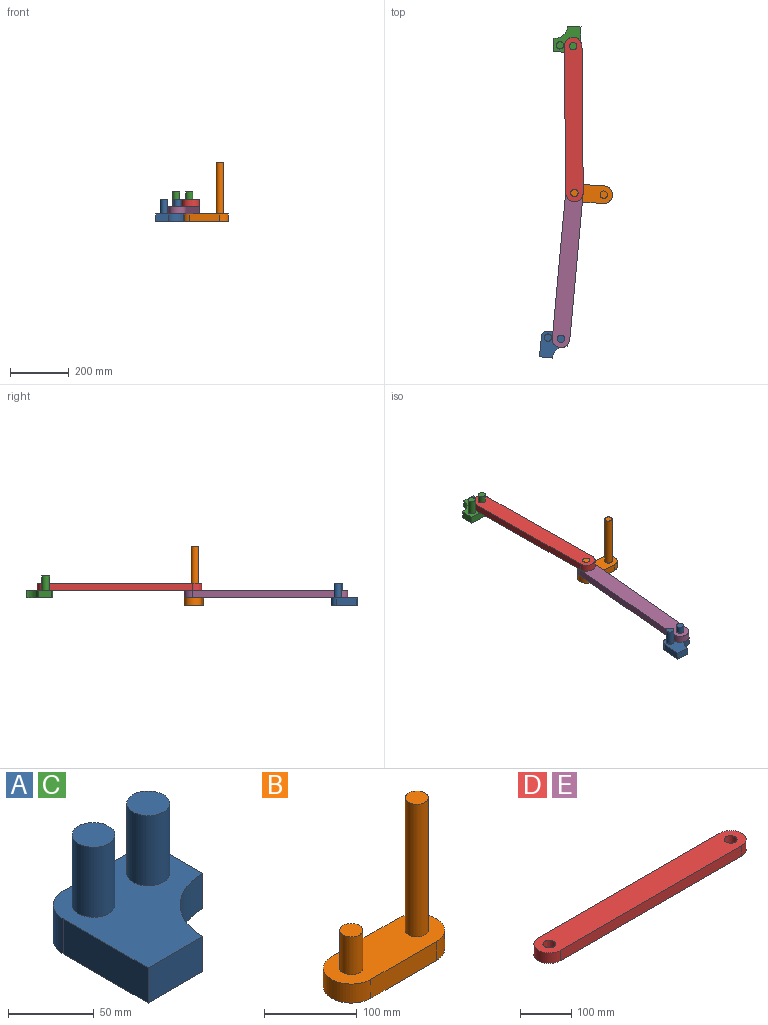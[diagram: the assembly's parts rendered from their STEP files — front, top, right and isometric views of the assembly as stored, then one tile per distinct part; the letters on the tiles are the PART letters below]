
ASSEMBLY  parts=5 mates=5
PART A: 12 faces, bbox 90x90x75 mm
  f0: plane 45x25mm, normal (1,0,0), area 1125mm2, adj f1,f4,f5,f6
  f1: plane 70x25mm, normal (0,1,0), area 1750mm2, adj f0,f4,f5,f7
  f2: plane 70x25mm, normal (-1,0,0), area 1750mm2, adj f3,f4,f5,f7
  f3: plane 45x25mm, normal (0,-1,0), area 1125mm2, adj f2,f4,f5,f6
  f4: plane 90x90mm, normal (0,0,1), area 5442mm2, adj f0,f1,f2,f3,f6,f7,f8,f10
  f5: plane 90x90mm, normal (0,0,-1), area 6423.7mm2, adj f0,f1,f2,f3,f6,f7
  f6: cylinder r=45mm len=45mm, axis (0,0,1), area 1767.1mm2, adj f0,f3,f4,f5
  f7: cylinder r=20mm len=25mm, axis (0,0,-1), area 785.4mm2, adj f1,f2,f4,f5
  f8: cylinder r=12.5mm len=50mm, axis (0,0,-1), area 3927mm2, adj f4,f9
  f9: plane 25x25mm, normal (0,0,1), area 490.9mm2, adj f8
  f10: cylinder r=12.5mm len=50mm, axis (0,0,-1), area 3927mm2, adj f4,f11
  f11: plane 25x25mm, normal (0,0,1), area 490.9mm2, adj f10
PART B: 10 faces, bbox 160x60x200 mm
  f0: plane 100x25mm, normal (0,1,0), area 2500mm2, adj f1,f3,f4,f5
  f1: cylinder r=30mm len=60mm, axis (0,0,-1), area 2356.2mm2, adj f0,f2,f4,f5
  f2: plane 100x25mm, normal (0,-1,0), area 2500mm2, adj f1,f3,f4,f5
  f3: cylinder r=30mm len=60mm, axis (0,0,-1), area 2356.2mm2, adj f0,f2,f4,f5
  f4: plane 160x60mm, normal (0,0,1), area 7845.7mm2, adj f0,f1,f2,f3,f6,f8
  f5: plane 160x60mm, normal (0,0,-1), area 8827.4mm2, adj f0,f1,f2,f3
  f6: cylinder r=12.5mm len=175mm, axis (0,0,-1), area 13744.5mm2, adj f4,f7
  f7: plane 25x25mm, normal (0,0,1), area 490.9mm2, adj f6
  f8: cylinder r=12.5mm len=50mm, axis (0,0,-1), area 3927mm2, adj f4,f9
  f9: plane 25x25mm, normal (0,0,1), area 490.9mm2, adj f8
PART C: same geometry as A
PART D: 8 faces, bbox 560x60x25 mm
  f0: plane 500x25mm, normal (0,1,0), area 12500mm2, adj f1,f5,f6,f7
  f1: cylinder r=30mm len=60mm, axis (0,0,-1), area 2356.2mm2, adj f0,f2,f6,f7
  f2: plane 500x25mm, normal (0,-1,0), area 12500mm2, adj f1,f5,f6,f7
  f3: cylinder r=12.5mm len=25mm, axis (0,0,-1), area 1963.5mm2, adj f6,f7
  f4: cylinder r=12.5mm len=25mm, axis (0,0,-1), area 1963.5mm2, adj f6,f7
  f5: cylinder r=30mm len=60mm, axis (0,0,-1), area 2356.2mm2, adj f0,f2,f6,f7
  f6: plane 560x60mm, normal (0,0,1), area 31845.7mm2, adj f0,f1,f2,f3,f4,f5
  f7: plane 560x60mm, normal (0,0,-1), area 31845.7mm2, adj f0,f1,f2,f3,f4,f5
PART E: same geometry as D
PLACE A rot(axis=(0,0,-1),5.2deg) t=(-148.94,-319.14,45.08)mm
PLACE B rot(axis=(0,0,-1),3.7deg) t=(-27.62,87.4,45.08)mm fixed
PLACE C rot(axis=(0,0,1),176.4deg) t=(-98.25,506.04,70.08)mm
PLACE D rot(axis=(0,0,-1),89.5deg) t=(-165.76,539.5,95.08)mm
PLACE E rot(axis=(0,0,1),84.8deg) t=(-34.36,-364.8,70.08)mm
MATE revolute D.f4 <-> B.f8  axis (0,0,-1) through (-77.52,90.63,120.08)mm
MATE parallel E.f6 <-> D.f6  axis (0,0,1) through (-100.3,-158.33,95.08)mm
MATE revolute A.f8 <-> E.f1  axis (0,0,-1) through (-123.09,-407.29,70.08)mm
MATE revolute E.f4 <-> B.f8  axis (0,0,-1) through (-77.52,90.63,70.08)mm
MATE revolute C.f10 <-> D.f1  axis (0,0,1) through (-81.7,590.61,95.08)mm
